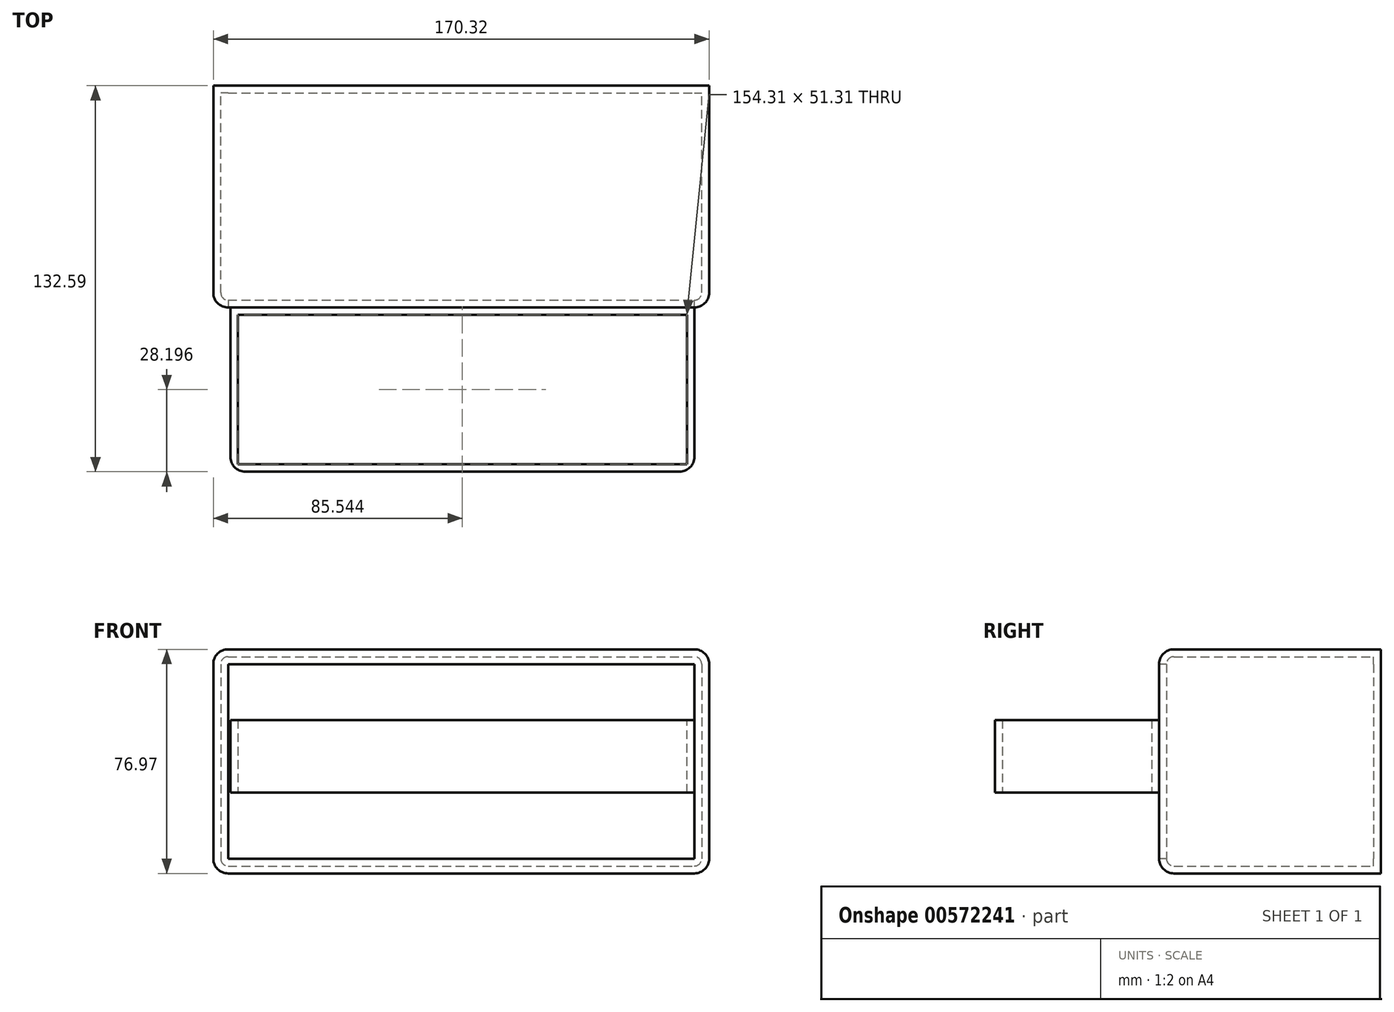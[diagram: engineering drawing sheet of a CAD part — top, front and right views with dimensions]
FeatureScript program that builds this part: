
annotation { "Feature Type Name" : "Feature", "Feature Type Description" : "" }
export const myFeature = defineFeature(function(context is Context, id is Id, definition is map)
    precondition{}
    {
        {
            var Q0;
            Q0=qCreatedBy(makeId("Front.planeOp"),FACE);
            var sketch = newSketch(context, id + "F0", { "sketchPlane" : qUnion([Q0])});
            skLineSegment(sketch, "E0.bottom", {"start": v(-97.95, 34.82) * mm, "end": v(72.37, 34.82) * mm});
            skLineSegment(sketch, "E0.top", {"start": v(-97.95, -42.15) * mm, "end": v(72.37, -42.15) * mm});
            skLineSegment(sketch, "E0.left", {"start": v(-97.95, 34.82) * mm, "end": v(-97.95, -42.15) * mm});
            skLineSegment(sketch, "E0.right", {"start": v(72.37, 34.82) * mm, "end": v(72.37, -42.15) * mm});
            skSolve(sketch);
        }
        {
            var Q0;
            Q0=makeQuery(id+"F0.imprint","IMPRINT",FACE,{"disambiguationData":[TD([[makeQuery(id+"F0.imprint","IMPRINT",EDGE,{"derivedFrom":sQuery(id+"F0.wireOp",EDGE,"E0.bottom")}),-1.0]])]});
            extrude(context, id + "F1", {"entities" : qUnion([Q0]), "depth" : 76.2 * mm, "offsetDistance" : 25.4 * mm});
        }
        {
            var Q0;
            Q0=makeQuery(id+"F1.opExtrude","CAP_EDGE",EDGE,{"disambiguationData":[OSD([sQuery(id+"F0.wireOp",EDGE,"E0.bottom")])],"isStart":false});
            var Q1;
            Q1=makeQuery(id+"F1.opExtrude","CAP_EDGE",EDGE,{"disambiguationData":[OSD([sQuery(id+"F0.wireOp",EDGE,"E0.top")])],"isStart":false});
            var Q2;
            Q2=makeQuery(id+"F1.opExtrude","CAP_EDGE",EDGE,{"disambiguationData":[OSD([sQuery(id+"F0.wireOp",EDGE,"E0.left")])],"isStart":false});
            var Q3;
            Q3=makeQuery(id+"F1.opExtrude","CAP_EDGE",EDGE,{"disambiguationData":[OSD([sQuery(id+"F0.wireOp",EDGE,"E0.right")])],"isStart":false});
            var Q4;
            Q4=makeQuery(id+"F1.opExtrude","SWEPT_EDGE",EDGE,{"disambiguationData":[OSD([sQuery(id+"F0.wireOp",EDGE,"E0.top"),sQuery(id+"F0.wireOp",EDGE,"E0.right")])]});
            var Q5;
            Q5=makeQuery(id+"F1.opExtrude","SWEPT_EDGE",EDGE,{"disambiguationData":[OSD([sQuery(id+"F0.wireOp",EDGE,"E0.bottom"),sQuery(id+"F0.wireOp",EDGE,"E0.right")])]});
            var Q6;
            Q6=makeQuery(id+"F1.opExtrude","SWEPT_EDGE",EDGE,{"disambiguationData":[OSD([sQuery(id+"F0.wireOp",EDGE,"E0.bottom"),sQuery(id+"F0.wireOp",EDGE,"E0.left")])]});
            var Q7;
            Q7=makeQuery(id+"F1.opExtrude","SWEPT_EDGE",EDGE,{"disambiguationData":[OSD([sQuery(id+"F0.wireOp",EDGE,"E0.top"),sQuery(id+"F0.wireOp",EDGE,"E0.left")])]});
            fillet(context, id + "F2", {"entities" : qUnion([Q0, Q1, Q2, Q3, Q4, Q5, Q6, Q7]), "radius" : 5.08 * mm, "tangentPropagation" : true, "allowEdgeOverflow" : false});
        }
        {
            var Q0;
            Q0=makeQuery(id+"F1.opExtrude","CAP_FACE",FACE,{"disambiguationData":[OSD([sQuery(id+"F0.wireOp",EDGE,"E0.bottom"),sQuery(id+"F0.wireOp",EDGE,"E0.top"),sQuery(id+"F0.wireOp",EDGE,"E0.left"),sQuery(id+"F0.wireOp",EDGE,"E0.right")])],"isStart":false});
            var sketch = newSketch(context, id + "F3", { "sketchPlane" : qUnion([Q0])});
            skSolve(sketch);
        }
        {
            var Q0;
            Q0=makeQuery(id+"F1.opExtrude","CAP_FACE",FACE,{"disambiguationData":[OSD([sQuery(id+"F0.wireOp",EDGE,"E0.bottom"),sQuery(id+"F0.wireOp",EDGE,"E0.top"),sQuery(id+"F0.wireOp",EDGE,"E0.left"),sQuery(id+"F0.wireOp",EDGE,"E0.right")])],"isStart":false});
            shell(context, id + "F4", {"entities" : qUnion([Q0]), "thickness" : 2.54 * mm});
        }
        {
            var Q0;
            {var subQ0=sQuery(id+"F0.wireOp",EDGE,"E0.right");var subQ1=sQuery(id+"F0.wireOp",EDGE,"E0.left");var subQ2=sQuery(id+"F0.wireOp",EDGE,"E0.top");var subQ3=sQuery(id+"F0.wireOp",EDGE,"E0.bottom");var subQ4=makeQuery(id+"F1.opExtrude","CAP_FACE",FACE,{"disambiguationData":[OSD([subQ3,subQ2,subQ1,subQ0])],"isStart":false});Q0=makeQuery(id+"F3.imprint","IMPRINT",FACE,{"disambiguationData":[TD([[makeQuery(id+"F3.imprint","IMPRINT",EDGE,{"derivedFrom":makeQuery(id+"F2.opFillet","BLEND_EDGE",EDGE,{"blendedFrom":[makeQuery(id+"F1.opExtrude","CAP_EDGE",EDGE,{"disambiguationData":[OSD([subQ3])],"isStart":false}),subQ4],"blendedInto":[subQ4]})}),1.0]])]});}
            var sketch = newSketch(context, id + "F5", { "sketchPlane" : qUnion([Q0])});
            skLineSegment(sketch, "E1.bottom", {"start": v(-92.1, 10.55) * mm, "end": v(67.47, 10.55) * mm});
            skLineSegment(sketch, "E1.top", {"start": v(-92.1, -14.43) * mm, "end": v(67.47, -14.43) * mm});
            skLineSegment(sketch, "E1.left", {"start": v(-92.1, 10.55) * mm, "end": v(-92.1, -14.43) * mm});
            skLineSegment(sketch, "E1.right", {"start": v(67.47, 10.55) * mm, "end": v(67.47, -14.43) * mm});
            skSolve(sketch);
        }
        {
            var Q0;
            {var subQ0=sQuery(id+"F5.wireOp",EDGE,"E1.left");Q0=makeQuery(id+"F5.imprint","IMPRINT",FACE,{"disambiguationData":[TD([[makeQuery(id+"F5.imprint","IMPRINT",EDGE,{"derivedFrom":subQ0}),1.0]])]});}
            extrude(context, id + "F6", {"entities" : qUnion([Q0]), "depth" : 56.4 * mm, "offsetDistance" : 25.4 * mm});
        }
        {
            var Q0;
            Q0=makeQuery(id+"F6.opExtrude","SWEPT_FACE",FACE,{"disambiguationData":[OSD([sQuery(id+"F5.wireOp",EDGE,"E1.bottom")])]});
            var Q1;
            Q1=makeQuery(id+"F6.opExtrude","SWEPT_FACE",FACE,{"disambiguationData":[OSD([sQuery(id+"F5.wireOp",EDGE,"E1.top")])]});
            shell(context, id + "F7", {"entities" : qUnion([Q0, Q1]), "thickness" : 2.54 * mm});
        }
        {
            var Q0;
            Q0=makeQuery(id+"F6.opExtrude","CAP_EDGE",EDGE,{"disambiguationData":[OSD([sQuery(id+"F0.wireOp",EDGE,"E0.bottom"),sQuery(id+"F0.wireOp",EDGE,"E0.top"),sQuery(id+"F0.wireOp",EDGE,"E0.left"),sQuery(id+"F0.wireOp",EDGE,"E0.right")])],"isStart":false});
            var Q1;
            Q1=makeQuery(id+"F6.opExtrude","CAP_EDGE",EDGE,{"disambiguationData":[OSD([sQuery(id+"F5.wireOp",EDGE,"E1.left")])],"isStart":false});
            fillet(context, id + "F8", {"entities" : qUnion([Q0, Q1]), "radius" : 5.08 * mm, "tangentPropagation" : true, "allowEdgeOverflow" : false});
        }
    });
